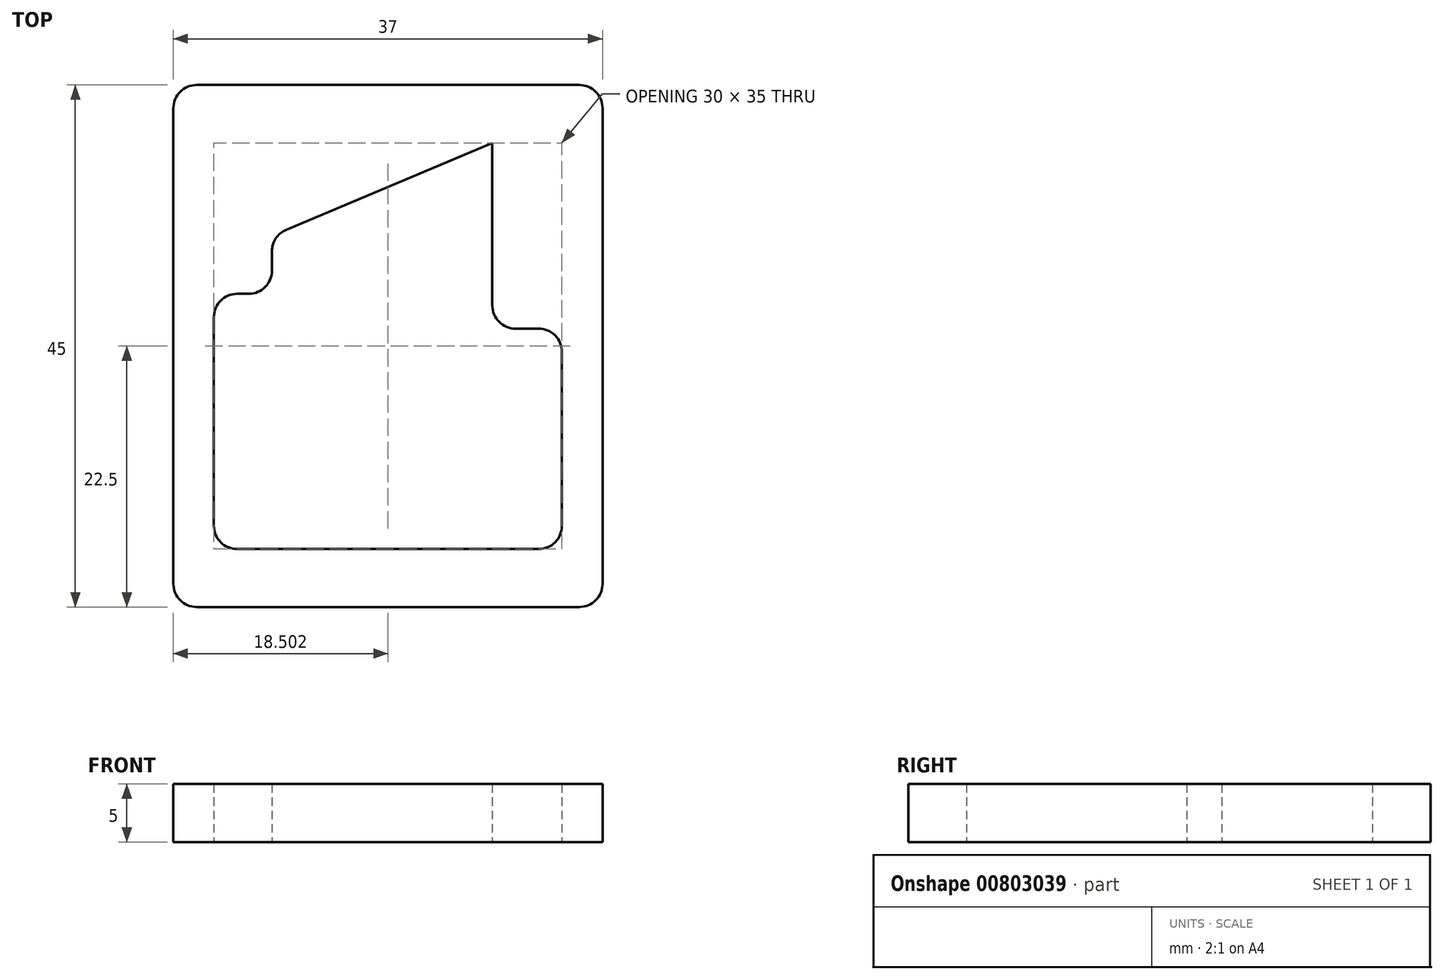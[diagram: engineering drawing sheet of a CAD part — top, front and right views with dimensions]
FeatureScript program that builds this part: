
annotation { "Feature Type Name" : "Feature", "Feature Type Description" : "" }
export const myFeature = defineFeature(function(context is Context, id is Id, definition is map)
    precondition{}
    {
        {
            var Q0;
            Q0=qCreatedBy(makeId("Top.planeOp"),FACE);
            var sketch = newSketch(context, id + "F0", { "sketchPlane" : qUnion([Q0])});
            skLineSegment(sketch, "E0.bottom", {"start": v(-18.56, 18) * mm, "end": v(14.44, 18) * mm});
            skLineSegment(sketch, "E0.top", {"start": v(-18.56, -27) * mm, "end": v(14.44, -27) * mm});
            skLineSegment(sketch, "E0.left", {"start": v(-20.56, 16) * mm, "end": v(-20.56, -25) * mm});
            skLineSegment(sketch, "E0.right", {"start": v(16.44, 16) * mm, "end": v(16.44, -25) * mm});
            skLineSegment(sketch, "E1", {"start": v(-17.06, -2) * mm, "end": v(-17.06, -20) * mm});
            skLineSegment(sketch, "E2", {"start": v(-15.06, -22) * mm, "end": v(10.94, -22) * mm});
            skLineSegment(sketch, "E3", {"start": v(12.94, -20) * mm, "end": v(12.94, -5) * mm});
            skLineSegment(sketch, "E4", {"start": v(-15.06, 0) * mm, "end": v(-14.06, 0) * mm});
            skLineSegment(sketch, "E5", {"start": v(-12.06, 2) * mm, "end": v(-12.06, 3.67) * mm});
            skLineSegment(sketch, "E6", {"start": v(10.94, -3) * mm, "end": v(8.94, -3) * mm});
            skLineSegment(sketch, "E7", {"start": v(6.94, -1) * mm, "end": v(6.94, 13) * mm});
            skLineSegment(sketch, "E8", {"start": v(6.94, 13) * mm, "end": v(-10.83, 5.52) * mm});
            skPoint(sketch, "E9.visualSharp", {"position": v(-20.56, 18) * mm});
            skArc(sketch, "E9.filletArc", {"start": v(-18.56, 18) * mm, "mid": v(-19.97, 17.41) * mm, "end": v(-20.56, 16) * mm});
            skPoint(sketch, "E10.visualSharp", {"position": v(16.44, 18) * mm});
            skArc(sketch, "E10.filletArc", {"start": v(16.44, 16) * mm, "mid": v(15.86, 17.41) * mm, "end": v(14.44, 18) * mm});
            skPoint(sketch, "E11.visualSharp", {"position": v(16.44, -27) * mm});
            skArc(sketch, "E11.filletArc", {"start": v(14.44, -27) * mm, "mid": v(15.86, -26.41) * mm, "end": v(16.44, -25) * mm});
            skPoint(sketch, "E12.visualSharp", {"position": v(-20.56, -27) * mm});
            skArc(sketch, "E12.filletArc", {"start": v(-20.56, -25) * mm, "mid": v(-19.97, -26.41) * mm, "end": v(-18.56, -27) * mm});
            skPoint(sketch, "E13.visualSharp", {"position": v(-17.06, -22) * mm});
            skArc(sketch, "E13.filletArc", {"start": v(-17.06, -20) * mm, "mid": v(-16.47, -21.41) * mm, "end": v(-15.06, -22) * mm});
            skPoint(sketch, "E14.visualSharp", {"position": v(12.94, -22) * mm});
            skArc(sketch, "E14.filletArc", {"start": v(10.94, -22) * mm, "mid": v(12.36, -21.41) * mm, "end": v(12.94, -20) * mm});
            skPoint(sketch, "E15.visualSharp", {"position": v(12.94, -3) * mm});
            skArc(sketch, "E15.filletArc", {"start": v(12.94, -5) * mm, "mid": v(12.36, -3.59) * mm, "end": v(10.94, -3) * mm});
            skPoint(sketch, "E16.visualSharp", {"position": v(6.94, -3) * mm});
            skArc(sketch, "E16.filletArc", {"start": v(6.94, -1) * mm, "mid": v(7.53, -2.41) * mm, "end": v(8.94, -3) * mm});
            skPoint(sketch, "E17.visualSharp", {"position": v(-17.06, 0) * mm});
            skArc(sketch, "E17.filletArc", {"start": v(-15.06, 0) * mm, "mid": v(-16.47, -0.59) * mm, "end": v(-17.06, -2) * mm});
            skPoint(sketch, "E18.visualSharp", {"position": v(-12.06, 0) * mm});
            skArc(sketch, "E18.filletArc", {"start": v(-14.06, 0) * mm, "mid": v(-12.64, 0.59) * mm, "end": v(-12.06, 2) * mm});
            skPoint(sketch, "E19.visualSharp", {"position": v(-12.06, 5) * mm});
            skArc(sketch, "E19.filletArc", {"start": v(-10.83, 5.52) * mm, "mid": v(-11.72, 4.78) * mm, "end": v(-12.06, 3.67) * mm});
            skSolve(sketch);
        }
        {
            var Q0;
            Q0=makeQuery(id+"F0.imprint","IMPRINT",FACE,{"disambiguationData":[TD([[makeQuery(id+"F0.imprint","IMPRINT",EDGE,{"derivedFrom":sQuery(id+"F0.wireOp",EDGE,"E0.bottom")}),-1.0]])]});
            extrude(context, id + "F1", {"entities" : qUnion([Q0]), "depth" : 5 * mm, "offsetDistance" : 25 * mm});
        }
    });
